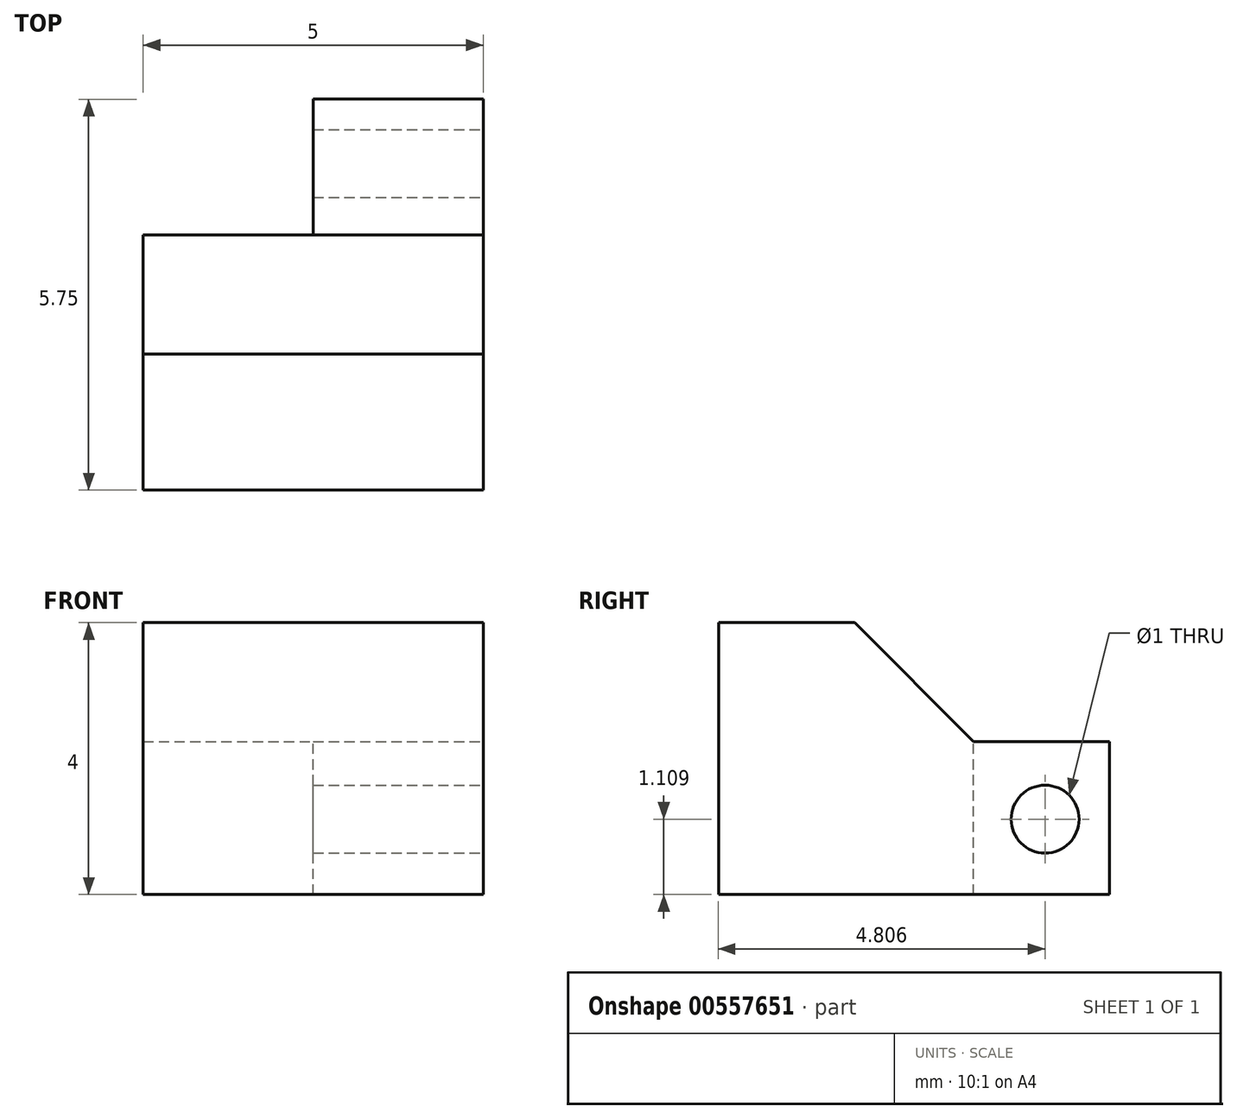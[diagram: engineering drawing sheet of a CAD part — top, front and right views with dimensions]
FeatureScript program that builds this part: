
annotation { "Feature Type Name" : "Feature", "Feature Type Description" : "" }
export const myFeature = defineFeature(function(context is Context, id is Id, definition is map)
    precondition{}
    {
        {
            var Q0;
            Q0=qCreatedBy(makeId("Right.planeOp"),FACE);
            var sketch = newSketch(context, id + "F0", { "sketchPlane" : qUnion([Q0])});
            skLineSegment(sketch, "E0", {"start": v(-1.93, 4) * mm, "end": v(0.07, 4) * mm});
            skLineSegment(sketch, "E1", {"start": v(1.82, 2.25) * mm, "end": v(0.07, 4) * mm});
            skLineSegment(sketch, "E2", {"start": v(1.82, 2.25) * mm, "end": v(3.82, 2.25) * mm});
            skLineSegment(sketch, "E3", {"start": v(3.82, 0) * mm, "end": v(3.82, 2.25) * mm});
            skLineSegment(sketch, "E4", {"start": v(3.82, 0) * mm, "end": v(1.82, 0) * mm});
            skLineSegment(sketch, "E5", {"start": v(1.82, 0) * mm, "end": v(1.82, 2.25) * mm});
            skLineSegment(sketch, "E6", {"start": v(1.82, 0) * mm, "end": v(-1.93, 0) * mm});
            skLineSegment(sketch, "E7", {"start": v(-1.93, 0) * mm, "end": v(-1.93, 4) * mm});
            skCircle(sketch, "E8", {"center": v(2.88, 1.1) * mm, "radius": 0.5 * mm});
            skSolve(sketch);
        }
        {
            var Q0;
            Q0=makeQuery(id+"F0.imprint","IMPRINT",FACE,{"disambiguationData":[TD([[makeQuery(id+"F0.imprint","IMPRINT",EDGE,{"derivedFrom":sQuery(id+"F0.wireOp",EDGE,"E0")}),-1.0]])]});
            extrude(context, id + "F1", {"entities" : qUnion([Q0]), "oppositeDirection" : true, "depth" : 5 * mm, "offsetDistance" : 25 * mm});
        }
        {
            var Q0;
            Q0=makeQuery(id+"F0.imprint","IMPRINT",FACE,{"disambiguationData":[TD([[makeQuery(id+"F0.imprint","IMPRINT",EDGE,{"derivedFrom":sQuery(id+"F0.wireOp",EDGE,"E2")}),-1.0]])]});
            extrude(context, id + "F2", {"entities" : qUnion([Q0]), "operationType" : NewBodyOperationType.ADD, "oppositeDirection" : true, "depth" : 2.5 * mm, "offsetDistance" : 25 * mm});
        }
    });
